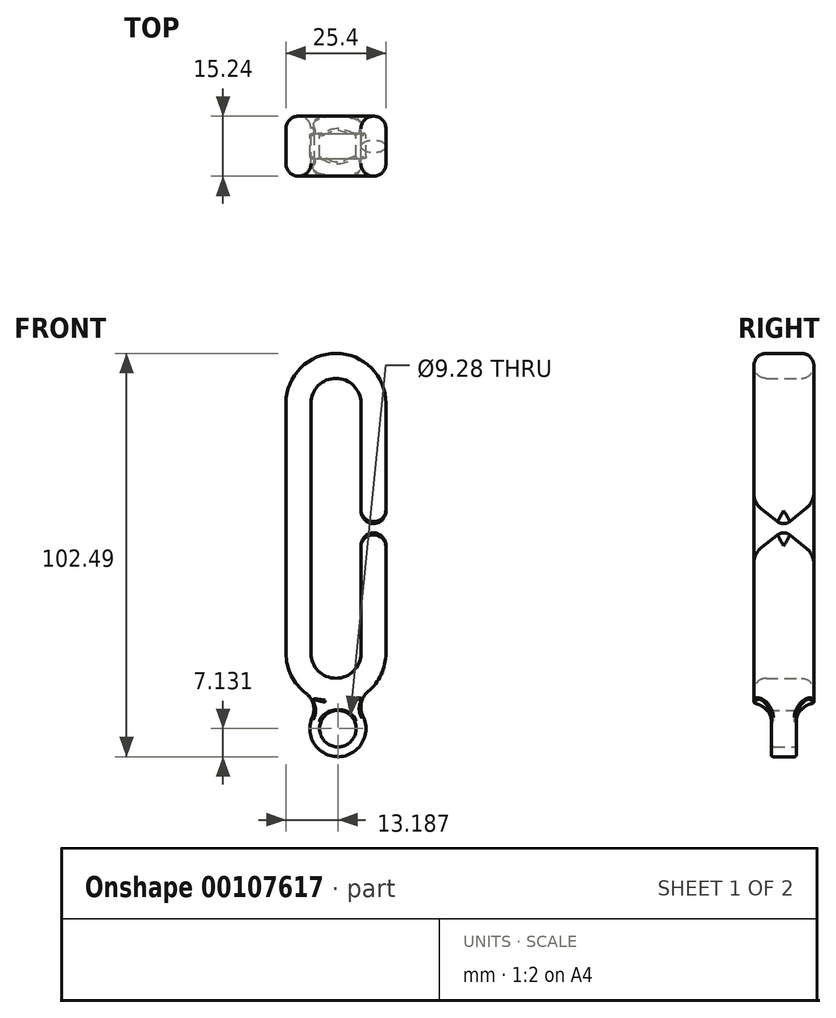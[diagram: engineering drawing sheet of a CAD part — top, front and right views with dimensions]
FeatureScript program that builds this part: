
annotation { "Feature Type Name" : "Feature", "Feature Type Description" : "" }
export const myFeature = defineFeature(function(context is Context, id is Id, definition is map)
    precondition{}
    {
        {
            var Q0;
            Q0=qCreatedBy(makeId("Front.planeOp"),FACE);
            var sketch = newSketch(context, id + "F0", { "sketchPlane" : qUnion([Q0])});
            skArc(sketch, "E0", {"start": v(0, 31.75) * mm, "mid": v(-12.7, 44.45) * mm, "end": v(-25.4, 31.75) * mm});
            skArc(sketch, "E1", {"start": v(-25.4, -31.75) * mm, "mid": v(-12.7, -44.45) * mm, "end": v(0, -31.75) * mm});
            skLineSegment(sketch, "E2.left", {"start": v(-25.4, 31.75) * mm, "end": v(-25.4, -31.75) * mm});
            skLineSegment(sketch, "E2.right", {"start": v(0, 31.75) * mm, "end": v(0, -31.75) * mm});
            skArc(sketch, "E3", {"start": v(-6.35, 31.75) * mm, "mid": v(-12.7, 38.1) * mm, "end": v(-19.05, 31.75) * mm});
            skArc(sketch, "E4", {"start": v(-19.05, -31.75) * mm, "mid": v(-12.7, -38.1) * mm, "end": v(-6.35, -31.75) * mm});
            skLineSegment(sketch, "E5", {"start": v(-19.05, 31.75) * mm, "end": v(-19.05, -31.75) * mm});
            skLineSegment(sketch, "E6", {"start": v(-6.35, 31.75) * mm, "end": v(-6.35, -31.75) * mm});
            skSolve(sketch);
        }
        {
            var Q0;
            Q0=makeQuery(id+"F0.imprint","IMPRINT",FACE,{"disambiguationData":[TD([[makeQuery(id+"F0.imprint","IMPRINT",EDGE,{"derivedFrom":sQuery(id+"F0.wireOp",EDGE,"E0")}),1.0]])]});
            extrude(context, id + "F1", {"entities" : qUnion([Q0]), "endBound" : BoundingType.SYMMETRIC, "depth" : 15.24 * mm});
        }
        {
            var Q0;
            Q0=qCreatedBy(makeId("Right.planeOp"),FACE);
            var sketch = newSketch(context, id + "F2", { "sketchPlane" : qUnion([Q0])});
            skLineSegment(sketch, "E7", {"start": v(0, 0.45) * mm, "end": v(-9.51, 7.88) * mm});
            skLineSegment(sketch, "E8", {"start": v(0, 0.45) * mm, "end": v(9.51, 8.19) * mm});
            skLineSegment(sketch, "E9.MirrorCS", {"start": v(0, -0.45) * mm, "end": v(-9.51, -7.88) * mm});
            skLineSegment(sketch, "E10.MirrorCS", {"start": v(0, -0.45) * mm, "end": v(9.51, -8.19) * mm});
            skLineSegment(sketch, "E11", {"start": v(-9.51, 7.88) * mm, "end": v(-9.51, -7.88) * mm});
            skLineSegment(sketch, "E12.MirrorCS", {"start": v(9.51, 8.19) * mm, "end": v(9.51, -8.19) * mm});
            skPoint(sketch, "E13.orphan", {"position": v(-9.51, 10.46) * mm});
            skPoint(sketch, "E14.orphan", {"position": v(-11.65, 9.55) * mm});
            skPoint(sketch, "E15.orphan", {"position": v(-11.65, -9.55) * mm});
            skPoint(sketch, "E16.orphan", {"position": v(-9.51, -11.62) * mm});
            skPoint(sketch, "E17.orphan", {"position": v(9.51, -11.62) * mm});
            skPoint(sketch, "E18.orphan", {"position": v(11.19, -9.55) * mm});
            skPoint(sketch, "E19.orphan", {"position": v(9.51, 10.46) * mm});
            skPoint(sketch, "E20.orphan", {"position": v(11.19, 9.55) * mm});
            skSolve(sketch);
        }
        {
            var Q0;
            Q0=makeQuery(id+"F2.imprint","IMPRINT",FACE,{"disambiguationData":[TD([[makeQuery(id+"F2.imprint","IMPRINT",EDGE,{"derivedFrom":sQuery(id+"F2.wireOp",EDGE,"E7")}),1.0]])]});
            var Q1;
            Q1=makeQuery(id+"F1.opExtrude","SWEPT_FACE",FACE,{"disambiguationData":[OSD([sQuery(id+"F0.wireOp",EDGE,"E6")])]});
            extrude(context, id + "F3", {"entities" : qUnion([Q0]), "operationType" : NewBodyOperationType.REMOVE, "endBound" : BoundingType.UP_TO_SURFACE, "oppositeDirection" : true, "endBoundEntityFace" : qUnion([Q1]), "depth" : 25.4 * mm});
        }
        {
            var Q0;
            Q0=makeQuery(id+"F3.boolean.opBoolean","COPY",EDGE,{"derivedFrom":makeQuery(id+"F3.opExtrude","SWEPT_EDGE",EDGE,{"disambiguationData":[OSD([sQuery(id+"F2.wireOp",EDGE,"E9.MirrorCS"),sQuery(id+"F2.wireOp",EDGE,"E10.MirrorCS")])]})});
            var Q1;
            Q1=makeQuery(id+"F3.boolean.opBoolean","COPY",EDGE,{"derivedFrom":makeQuery(id+"F3.opExtrude","SWEPT_EDGE",EDGE,{"disambiguationData":[OSD([sQuery(id+"F2.wireOp",EDGE,"E7"),sQuery(id+"F2.wireOp",EDGE,"E8")])]})});
            fillet(context, id + "F4", {"entities" : qUnion([Q0, Q1]), "radius" : 2.54 * mm, "tangentPropagation" : true, "allowEdgeOverflow" : false});
        }
        {
            var Q0;
            Q0=qCreatedBy(makeId("Front.planeOp"),FACE);
            var sketch = newSketch(context, id + "F5", { "sketchPlane" : qUnion([Q0])});
            skCircle(sketch, "E21", {"center": v(-12.21, -50.9) * mm, "radius": 7.13 * mm});
            skCircle(sketch, "E22", {"center": v(-12.21, -50.9) * mm, "radius": 4.64 * mm});
            skSolve(sketch);
        }
        {
            var Q0;
            Q0=makeQuery(id+"F5.imprint","IMPRINT",FACE,{"disambiguationData":[TD([[makeQuery(id+"F5.imprint","IMPRINT",EDGE,{"derivedFrom":sQuery(id+"F5.wireOp",EDGE,"E21")}),1.0]])]});
            extrude(context, id + "F6", {"entities" : qUnion([Q0]), "operationType" : NewBodyOperationType.ADD, "endBound" : BoundingType.SYMMETRIC, "depth" : 6.35 * mm});
        }
        {
            var Q0;
            Q0=makeQuery(id+"F6.boolean.opBoolean","INTERSECT",EDGE,{"derivedFrom":[makeQuery(id+"F1.opExtrude","SWEPT_FACE",FACE,{"disambiguationData":[OSD([sQuery(id+"F0.wireOp",EDGE,"E1")])]}),makeQuery(id+"F6.opExtrude","CAP_FACE",FACE,{"disambiguationData":[OSD([sQuery(id+"F5.wireOp",EDGE,"E21"),sQuery(id+"F5.wireOp",EDGE,"E22")])],"isStart":false})]});
            var Q1;
            Q1=makeQuery(id+"F6.boolean.opBoolean","INTERSECT",EDGE,{"disambiguationData":[OD(1.0)],"derivedFrom":[makeQuery(id+"F1.opExtrude","SWEPT_FACE",FACE,{"disambiguationData":[OSD([sQuery(id+"F0.wireOp",EDGE,"E1")])]}),makeQuery(id+"F6.opExtrude","SWEPT_FACE",FACE,{"disambiguationData":[OSD([sQuery(id+"F5.wireOp",EDGE,"E21")])]})]});
            var Q2;
            Q2=makeQuery(id+"F6.boolean.opBoolean","INTERSECT",EDGE,{"derivedFrom":[makeQuery(id+"F1.opExtrude","SWEPT_FACE",FACE,{"disambiguationData":[OSD([sQuery(id+"F0.wireOp",EDGE,"E1")])]}),makeQuery(id+"F6.opExtrude","CAP_FACE",FACE,{"disambiguationData":[OSD([sQuery(id+"F5.wireOp",EDGE,"E21"),sQuery(id+"F5.wireOp",EDGE,"E22")])],"isStart":true})]});
            var Q3;
            Q3=makeQuery(id+"F6.boolean.opBoolean","INTERSECT",EDGE,{"disambiguationData":[OD(0.0)],"derivedFrom":[makeQuery(id+"F1.opExtrude","SWEPT_FACE",FACE,{"disambiguationData":[OSD([sQuery(id+"F0.wireOp",EDGE,"E1")])]}),makeQuery(id+"F6.opExtrude","SWEPT_FACE",FACE,{"disambiguationData":[OSD([sQuery(id+"F5.wireOp",EDGE,"E21")])]})]});
            fillet(context, id + "F7", {"entities" : qUnion([Q0, Q1, Q2, Q3]), "radius" : 5.08 * mm, "tangentPropagation" : true, "allowEdgeOverflow" : false});
        }
        {
            var Q0;
            Q0=makeQuery(id+"F3.boolean.opBoolean","INTERSECT",EDGE,{"derivedFrom":[makeQuery(id+"F1.opExtrude","CAP_FACE",FACE,{"disambiguationData":[OSD([sQuery(id+"F0.wireOp",EDGE,"E0"),sQuery(id+"F0.wireOp",EDGE,"E1"),sQuery(id+"F0.wireOp",EDGE,"E2.left"),sQuery(id+"F0.wireOp",EDGE,"E2.right"),sQuery(id+"F0.wireOp",EDGE,"E3"),sQuery(id+"F0.wireOp",EDGE,"E4"),sQuery(id+"F0.wireOp",EDGE,"E5"),sQuery(id+"F0.wireOp",EDGE,"E6")])],"isStart":true}),makeQuery(id+"F3.opExtrude","SWEPT_FACE",FACE,{"disambiguationData":[OSD([sQuery(id+"F2.wireOp",EDGE,"E8")])]})]});
            var Q1;
            Q1=makeQuery(id+"F3.boolean.opBoolean","INTERSECT",EDGE,{"derivedFrom":[makeQuery(id+"F1.opExtrude","CAP_FACE",FACE,{"disambiguationData":[OSD([sQuery(id+"F0.wireOp",EDGE,"E0"),sQuery(id+"F0.wireOp",EDGE,"E1"),sQuery(id+"F0.wireOp",EDGE,"E2.left"),sQuery(id+"F0.wireOp",EDGE,"E2.right"),sQuery(id+"F0.wireOp",EDGE,"E3"),sQuery(id+"F0.wireOp",EDGE,"E4"),sQuery(id+"F0.wireOp",EDGE,"E5"),sQuery(id+"F0.wireOp",EDGE,"E6")])],"isStart":true}),makeQuery(id+"F3.opExtrude","SWEPT_FACE",FACE,{"disambiguationData":[OSD([sQuery(id+"F2.wireOp",EDGE,"E10.MirrorCS")])]})]});
            var Q2;
            Q2=makeQuery(id+"F3.boolean.opBoolean","INTERSECT",EDGE,{"derivedFrom":[makeQuery(id+"F1.opExtrude","CAP_FACE",FACE,{"disambiguationData":[OSD([sQuery(id+"F0.wireOp",EDGE,"E0"),sQuery(id+"F0.wireOp",EDGE,"E1"),sQuery(id+"F0.wireOp",EDGE,"E2.left"),sQuery(id+"F0.wireOp",EDGE,"E2.right"),sQuery(id+"F0.wireOp",EDGE,"E3"),sQuery(id+"F0.wireOp",EDGE,"E4"),sQuery(id+"F0.wireOp",EDGE,"E5"),sQuery(id+"F0.wireOp",EDGE,"E6")])],"isStart":false}),makeQuery(id+"F3.opExtrude","SWEPT_FACE",FACE,{"disambiguationData":[OSD([sQuery(id+"F2.wireOp",EDGE,"E9.MirrorCS")])]})]});
            var Q3;
            Q3=makeQuery(id+"F3.boolean.opBoolean","INTERSECT",EDGE,{"derivedFrom":[makeQuery(id+"F1.opExtrude","CAP_FACE",FACE,{"disambiguationData":[OSD([sQuery(id+"F0.wireOp",EDGE,"E0"),sQuery(id+"F0.wireOp",EDGE,"E1"),sQuery(id+"F0.wireOp",EDGE,"E2.left"),sQuery(id+"F0.wireOp",EDGE,"E2.right"),sQuery(id+"F0.wireOp",EDGE,"E3"),sQuery(id+"F0.wireOp",EDGE,"E4"),sQuery(id+"F0.wireOp",EDGE,"E5"),sQuery(id+"F0.wireOp",EDGE,"E6")])],"isStart":false}),makeQuery(id+"F3.opExtrude","SWEPT_FACE",FACE,{"disambiguationData":[OSD([sQuery(id+"F2.wireOp",EDGE,"E7")])]})]});
            fillet(context, id + "F8", {"entities" : qUnion([Q0, Q1, Q2, Q3]), "radius" : 5.08 * mm, "tangentPropagation" : true, "allowEdgeOverflow" : false});
        }
        {
            var Q0;
            {var subQ0=sQuery(id+"F0.wireOp",EDGE,"E2.right");var subQ1=sQuery(id+"F0.wireOp",EDGE,"E1");Q0=makeQuery(id+"F3.boolean.opBoolean","SPLIT",EDGE,{"disambiguationData":[TD([makeQuery(id+"F1.opExtrude","SWEPT_FACE",FACE,{"disambiguationData":[OSD([subQ1])]})])],"derivedFrom":makeQuery(id+"F1.opExtrude","CAP_EDGE",EDGE,{"disambiguationData":[OSD([subQ0])],"isStart":true})});}
            var Q1;
            Q1=makeQuery(id+"F1.opExtrude","CAP_EDGE",EDGE,{"disambiguationData":[OSD([sQuery(id+"F0.wireOp",EDGE,"E1")])],"isStart":true});
            var Q2;
            {var subQ0=sQuery(id+"F0.wireOp",EDGE,"E6");var subQ1=sQuery(id+"F0.wireOp",EDGE,"E4");Q2=makeQuery(id+"F3.boolean.opBoolean","SPLIT",EDGE,{"disambiguationData":[TD([makeQuery(id+"F1.opExtrude","SWEPT_FACE",FACE,{"disambiguationData":[OSD([subQ1])]})])],"derivedFrom":makeQuery(id+"F1.opExtrude","CAP_EDGE",EDGE,{"disambiguationData":[OSD([subQ0])],"isStart":true})});}
            fillet(context, id + "F9", {"entities" : qUnion([Q0, Q1, Q2]), "radius" : 3.17 * mm, "tangentPropagation" : true, "allowEdgeOverflow" : false});
        }
        {
            var Q0;
            Q0=makeQuery(id+"F6.opExtrude","CAP_FACE",FACE,{"disambiguationData":[OSD([sQuery(id+"F5.wireOp",EDGE,"E21"),sQuery(id+"F5.wireOp",EDGE,"E22")])],"isStart":true});
            var Q1;
            Q1=makeQuery(id+"F6.opExtrude","CAP_FACE",FACE,{"disambiguationData":[OSD([sQuery(id+"F5.wireOp",EDGE,"E21"),sQuery(id+"F5.wireOp",EDGE,"E22")])],"isStart":false});
            fillet(context, id + "F10", {"entities" : qUnion([Q0, Q1]), "radius" : 0.5 * mm, "tangentPropagation" : true, "allowEdgeOverflow" : false});
        }
    });
